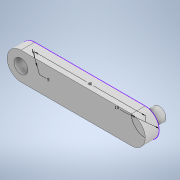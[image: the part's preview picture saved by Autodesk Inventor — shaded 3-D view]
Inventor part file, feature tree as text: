
AUTODESK INVENTOR PART (.ipt)
format: ipt  version: 2022 (Build 260153000, 153)  size: 107,520 bytes
history: native  units: mm
features: extrude x2, sketch x1
ambient origin geometry x8: Origin, YZ Plane, XZ Plane, XY Plane, X Axis, Y Axis, Z Axis, Center Point
bodies: Solid1 (feature_tree)
feature tree (3):
  sketch  "Sketch1"  dims[d0=40.0mm d1=10.0mm d2=5.0mm d3=5.0mm d4=0.0mm d5=5.0mm d6=0.0mm]
  extrude  "Extrusion1"  Depth=10.0mm
  extrude  "Extrusion2"  Depth=5.0mm
